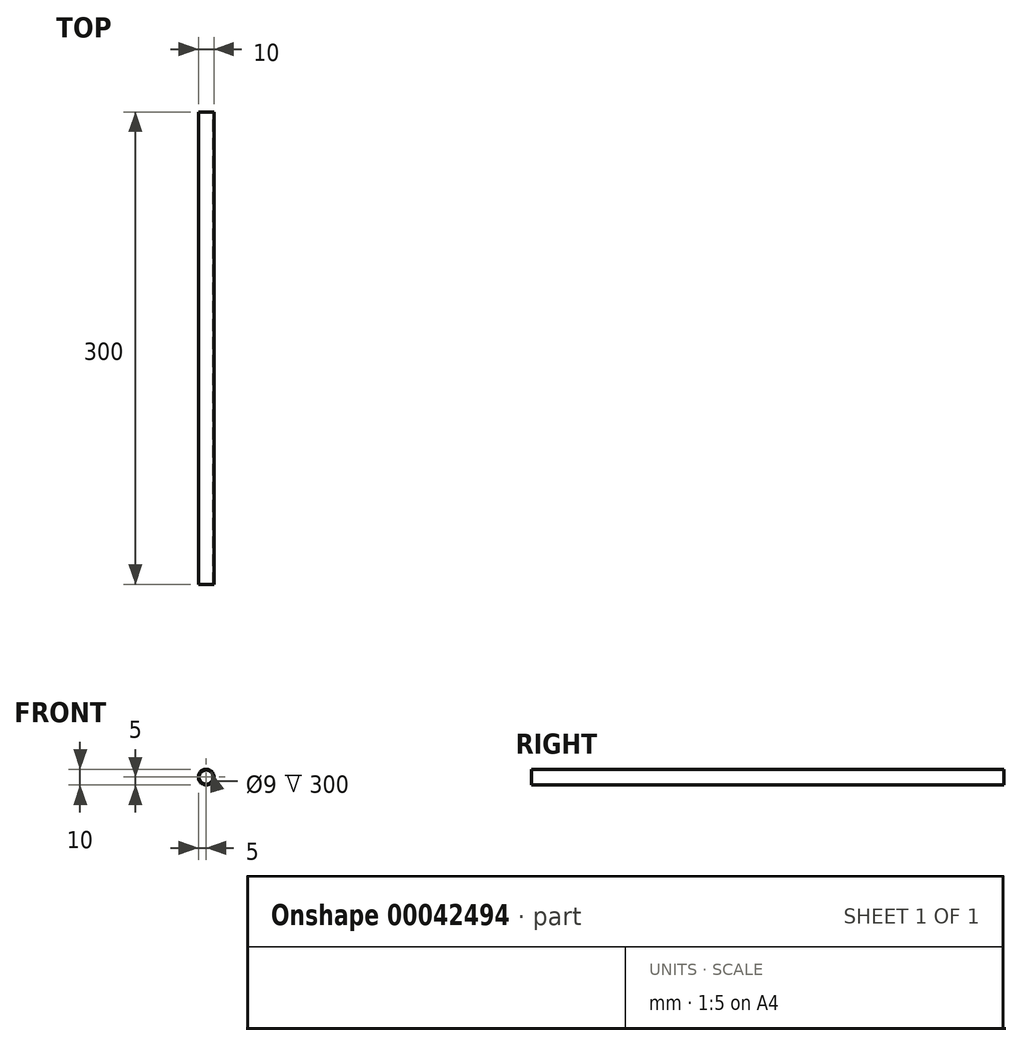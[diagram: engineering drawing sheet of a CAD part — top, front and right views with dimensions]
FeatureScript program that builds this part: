
annotation { "Feature Type Name" : "Feature", "Feature Type Description" : "" }
export const myFeature = defineFeature(function(context is Context, id is Id, definition is map)
    precondition{}
    {
        {
            var Q0;
            Q0=qCreatedBy(makeId("Front.planeOp"),FACE);
            var sketch = newSketch(context, id + "F0", { "sketchPlane" : qUnion([Q0])});
            skCircle(sketch, "E0", {"center": v(0, 0) * mm, "radius": 5 * mm});
            skCircle(sketch, "E1", {"center": v(0, 0) * mm, "radius": 4.5 * mm});
            skSolve(sketch);
        }
        {
            var Q0;
            Q0 = qSketchRegion(id + "F0", true);
            extrude(context, id + "F1", {"entities" : qUnion([Q0]), "depth" : 300 * mm});
        }
    });
